# Revit family: Building-QuadriIEC309-GEWISS-68QDIN-QUADRI-PRESE-5MOD_1PRESA
name_source: partatom
category: Apparecchi elettrici
units: mm (PartAtom-declared; Revit-internal decimal feet)

## family parameters
Condiviso = No
Host = Superficie
Mantenere orientamento annotazione = Sì
Punto di calcolo locali = Sì
Quota connettore circolare = Usa diametro
Taglio con vuoti quando caricato = No
Tipo di parte = Normale

## types (1)
- GW68017N - Q-DIN 5M 1FLANGIA PR.16A IP65
    Catalogo = BUILDING
    Catalogo Serie = 68 QDIN
    Classe isolamento = II
    Codice EAN = 8011564744851
    Codice Electrocod = 2242
    Colore = Grigio RAL 7035
    Conformità normativa = EN 60208 - EN 60670-1 - IEC 60670-24
    Descrizione = Q-DIN 5M 1FLANGIA PR.16A IP65
    Glow Wire Test = 650°C
    Grado di protezione = IP65
    IDF = ecafc8a6-5119-45a7-aebb-aaca6b32a7d0
    IDT = ee7be3a0-8e2c-4958-911f-c8bff68fcaa4
    Immagine tipo = GW68017N.jpg
    Modello = GW68017N
    N. coperchi ciechi in dotazione = -
    N. mod. EN 50022 = 5
    N. prese alloggiabili = 1 IEC 309 16 A IP44/67
    POMELLO = bianco
    PRESA = rosso
    Potenza dissipabile A (W) = 10
    Potenza dissipabile B (W) = 37
    Produttore = GEWISS S.p.A.
    Prospetto di default = 1219 mm
    Resistenza agli urti = IK08
    SEO = Quadretto
    STRUTTURA = RAL - 7035
    STRUTTURA ALTA = Poche
    Scheda Tecnica = https://www.gewiss.com
    Spostamento_S = 1000 mm  [stored 3.28084 ft]
    Temperatura di utilizzo = -25 +40 °C
    Termopressione con biglia = 70 °C
    Tipo versione = Vuoto
    Tipologia di installazione = Da parete
    URL = https://www.gewiss.com
    VETRO = Vetro
    Versione file RFA = 21.5
    l_Moduli = 95 mm
    n_moduli = 5 mm  [stored 0.0164042 ft]

note: [stored X ft] marks values corroborated as IEEE doubles in the binary element streams (Revit-internal decimal feet)

## geometry (parser evidence)
native form markers: Sweep x3
no freeform markers — native parametric forms only
